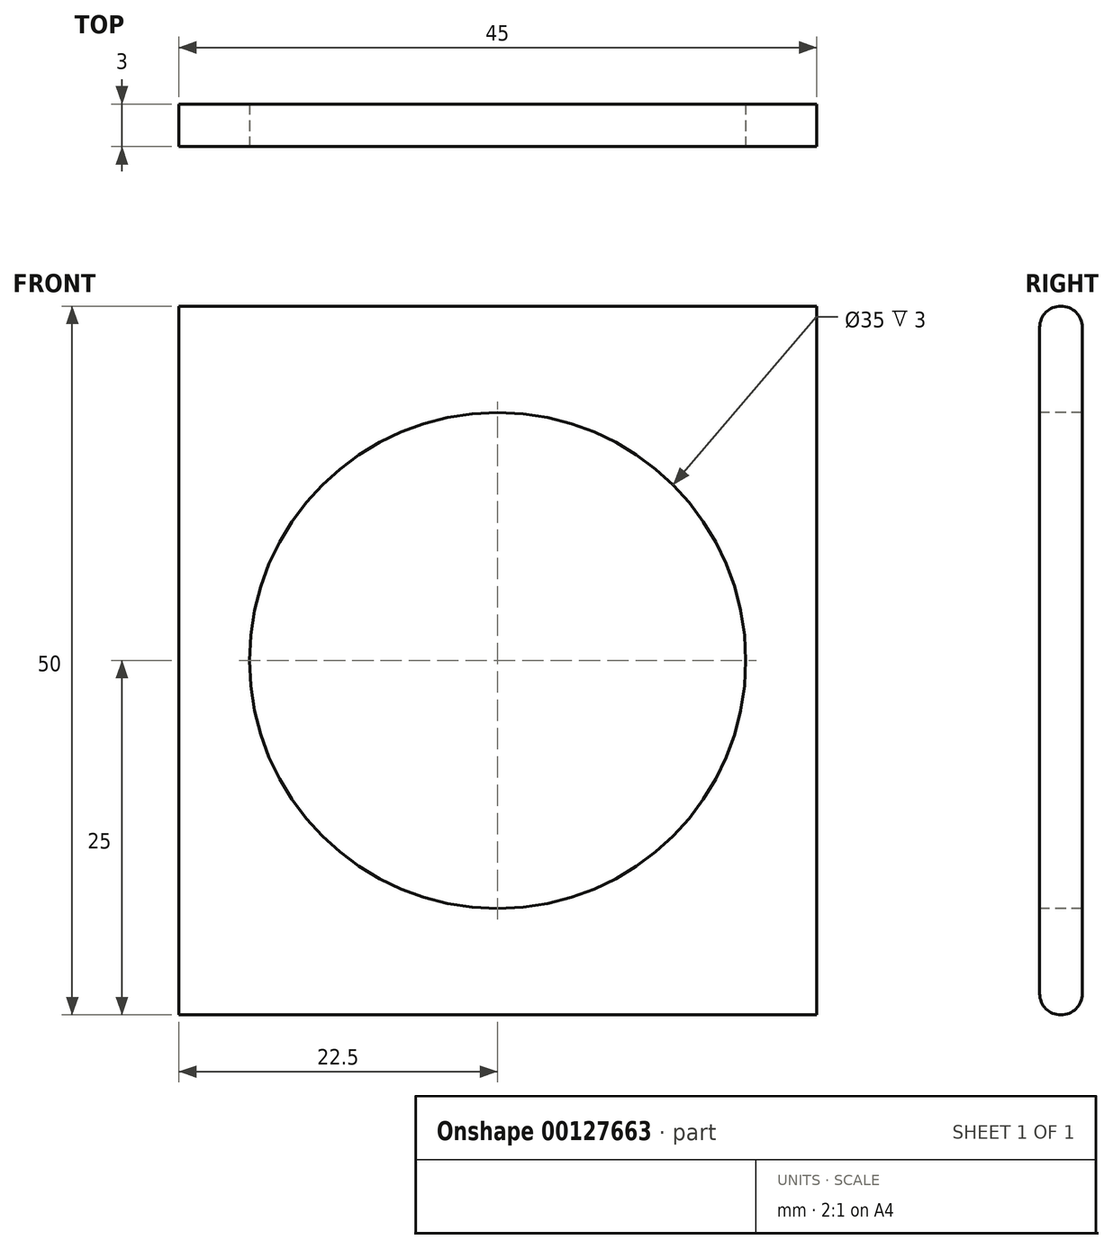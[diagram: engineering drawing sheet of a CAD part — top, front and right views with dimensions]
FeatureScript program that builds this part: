
annotation { "Feature Type Name" : "Feature", "Feature Type Description" : "" }
export const myFeature = defineFeature(function(context is Context, id is Id, definition is map)
    precondition{}
    {
        {
            var Q0;
            Q0=qCreatedBy(makeId("Right.planeOp"),FACE);
            var sketch = newSketch(context, id + "F0", { "sketchPlane" : qUnion([Q0])});
            skLineSegment(sketch, "E0", {"start": v(0, 25) * mm, "end": v(0, -25) * mm});
            skLineSegment(sketch, "E1", {"start": v(0, -25) * mm, "end": v(-3, -25) * mm});
            skLineSegment(sketch, "E2", {"start": v(-3, -25) * mm, "end": v(-3, -21.25) * mm});
            skLineSegment(sketch, "E3", {"start": v(-3, -21.25) * mm, "end": v(-9, -21.25) * mm});
            skLineSegment(sketch, "E4", {"start": v(-9, -21.25) * mm, "end": v(-9, 21.25) * mm});
            skLineSegment(sketch, "E5", {"start": v(-9, 21.25) * mm, "end": v(-3, 21.25) * mm});
            skLineSegment(sketch, "E6", {"start": v(-3, 21.25) * mm, "end": v(-3, 25) * mm});
            skLineSegment(sketch, "E7", {"start": v(-3, 25) * mm, "end": v(0, 25) * mm});
            skSolve(sketch);
        }
        {
            var Q0;
            Q0=qSketchRegion(id+"F0",true);
            extrude(context, id + "F1", {"entities" : qUnion([Q0]), "endBound" : BoundingType.SYMMETRIC, "depth" : 45 * mm});
        }
        {
            var Q0;
            Q0=makeQuery(id+"F1.opExtrude","SWEPT_FACE",FACE,{"disambiguationData":[OSD([sQuery(id+"F0.wireOp",EDGE,"E4")])]});
            var sketch = newSketch(context, id + "F2", { "sketchPlane" : qUnion([Q0])});
            skCircle(sketch, "E8", {"center": v(0, 0) * mm, "radius": 18.6 * mm});
            skSolve(sketch);
        }
        {
            var Q0;
            Q0=qSketchRegion(id+"F2",true);
            extrude(context, id + "F3", {"entities" : qUnion([Q0]), "operationType" : NewBodyOperationType.REMOVE, "oppositeDirection" : true, "depth" : 6 * mm});
        }
        {
            var Q0;
            Q0=makeQuery(id+"F3.boolean.opBoolean","COPY",FACE,{"derivedFrom":makeQuery(id+"F3.opExtrude","CAP_FACE",FACE,{"disambiguationData":[OSD([sQuery(id+"F2.wireOp",EDGE,"E8")])],"isStart":false})});
            var sketch = newSketch(context, id + "F4", { "sketchPlane" : qUnion([Q0])});
            skCircle(sketch, "E9", {"center": v(0, 0) * mm, "radius": 17.5 * mm});
            skSolve(sketch);
        }
        {
            var Q0;
            Q0=qSketchRegion(id+"F4",true);
            extrude(context, id + "F5", {"entities" : qUnion([Q0]), "operationType" : NewBodyOperationType.REMOVE, "endBound" : BoundingType.UP_TO_NEXT, "oppositeDirection" : true, "depth" : 25 * mm});
        }
        {
            var Q0;
            Q0=makeQuery(id+"F1.opExtrude","SWEPT_FACE",FACE,{"disambiguationData":[OSD([sQuery(id+"F0.wireOp",EDGE,"E4")])]});
            var sketch = newSketch(context, id + "F6", { "sketchPlane" : qUnion([Q0])});
            skLineSegment(sketch, "E10", {"start": v(0, 42.2) * mm, "end": v(0, -42.2) * mm, "construction": true});
            skLineSegment(sketch, "E11", {"start": v(-1.5, 21.05) * mm, "end": v(-1.68, 21.11) * mm});
            skLineSegment(sketch, "E12", {"start": v(-1.6, 25.84) * mm, "end": v(0.72, 26.6) * mm});
            skLineSegment(sketch, "E13", {"start": v(0.72, 28.5) * mm, "end": v(-3.1, 29.74) * mm});
            skLineSegment(sketch, "E14", {"start": v(-3.57, 34.29) * mm, "end": v(2.83, 37.92) * mm});
            skLineSegment(sketch, "E15", {"start": v(2.64, 39.74) * mm, "end": v(-4.93, 42.2) * mm});
            skLineSegment(sketch, "E16", {"start": v(-8.5, 31.5) * mm, "end": v(-8.5, 23.6) * mm, "construction": true});
            skLineSegment(sketch, "E17", {"start": v(-1.13, 24.41) * mm, "end": v(1.18, 25.17) * mm});
            skLineSegment(sketch, "E18", {"start": v(1.18, 29.92) * mm, "end": v(-2.64, 31.16) * mm});
            skLineSegment(sketch, "E19", {"start": v(-2.83, 32.99) * mm, "end": v(3.57, 36.61) * mm});
            skLineSegment(sketch, "E20", {"start": v(3.1, 41.17) * mm, "end": v(-0.08, 42.2) * mm});
            skLineSegment(sketch, "E21", {"start": v(8.5, 39.41) * mm, "end": v(8.5, 27.54) * mm, "construction": true});
            skLineSegment(sketch, "E22", {"start": v(-4.93, 42.2) * mm, "end": v(-0.08, 42.2) * mm});
            skPoint(sketch, "E23.visualSharp", {"position": v(-4.8, 31.87) * mm});
            skArc(sketch, "E23.filletArc", {"start": v(-2.83, 32.99) * mm, "mid": v(-3.33, 32.01) * mm, "end": v(-2.64, 31.16) * mm});
            skPoint(sketch, "E24.visualSharp", {"position": v(-4.56, 23.3) * mm});
            skArc(sketch, "E24.filletArc", {"start": v(-1.13, 24.41) * mm, "mid": v(-1.82, 23.48) * mm, "end": v(-1.16, 22.52) * mm});
            skPoint(sketch, "E25.visualSharp", {"position": v(3.65, 27.54) * mm});
            skArc(sketch, "E25.filletArc", {"start": v(0.72, 26.6) * mm, "mid": v(1.4, 27.54) * mm, "end": v(0.72, 28.5) * mm});
            skPoint(sketch, "E26.visualSharp", {"position": v(4.8, 39.04) * mm});
            skArc(sketch, "E26.filletArc", {"start": v(2.83, 37.92) * mm, "mid": v(3.33, 38.89) * mm, "end": v(2.64, 39.74) * mm});
            skPoint(sketch, "E27.visualSharp", {"position": v(8.5, 39.41) * mm});
            skArc(sketch, "E27.filletArc", {"start": v(3.57, 36.61) * mm, "mid": v(4.82, 39.04) * mm, "end": v(3.1, 41.17) * mm});
            skPoint(sketch, "E28.visualSharp", {"position": v(-8.5, 31.5) * mm});
            skArc(sketch, "E28.filletArc", {"start": v(-3.57, 34.29) * mm, "mid": v(-4.82, 31.86) * mm, "end": v(-3.1, 29.74) * mm});
            skPoint(sketch, "E29.visualSharp", {"position": v(8.5, 27.54) * mm});
            skArc(sketch, "E29.filletArc", {"start": v(1.18, 25.17) * mm, "mid": v(2.9, 27.54) * mm, "end": v(1.18, 29.92) * mm});
            skPoint(sketch, "E30.visualSharp", {"position": v(-8.5, 23.6) * mm});
            skArc(sketch, "E30.filletArc", {"start": v(-1.6, 25.84) * mm, "mid": v(-3.32, 23.5) * mm, "end": v(-1.68, 21.11) * mm});
            skLineSegment(sketch, "E31", {"start": v(0, 0) * mm, "end": v(22.5, 0) * mm, "construction": true});
            skArc(sketch, "E32.MirrorCS", {"start": v(-2.83, -32.99) * mm, "mid": v(-3.33, -32.01) * mm, "end": v(-2.64, -31.16) * mm});
            skArc(sketch, "E33.MirrorCS", {"start": v(2.83, -37.92) * mm, "mid": v(3.33, -38.89) * mm, "end": v(2.64, -39.74) * mm});
            skArc(sketch, "E34.MirrorCS", {"start": v(-1.13, -24.41) * mm, "mid": v(-1.82, -23.48) * mm, "end": v(-1.16, -22.52) * mm});
            skLineSegment(sketch, "E35.MirrorCS", {"start": v(3.1, -41.17) * mm, "end": v(-0.08, -42.2) * mm});
            skLineSegment(sketch, "E36.MirrorCS", {"start": v(-1.5, -21.05) * mm, "end": v(-1.68, -21.11) * mm});
            skArc(sketch, "E37.MirrorCS", {"start": v(0.72, -26.6) * mm, "mid": v(1.4, -27.54) * mm, "end": v(0.72, -28.5) * mm});
            skArc(sketch, "E38.MirrorCS", {"start": v(1.18, -25.17) * mm, "mid": v(2.9, -27.54) * mm, "end": v(1.18, -29.92) * mm});
            skArc(sketch, "E39.MirrorCS", {"start": v(3.57, -36.61) * mm, "mid": v(4.82, -39.04) * mm, "end": v(3.1, -41.17) * mm});
            skArc(sketch, "E40.MirrorCS", {"start": v(-3.57, -34.29) * mm, "mid": v(-4.82, -31.86) * mm, "end": v(-3.1, -29.74) * mm});
            skLineSegment(sketch, "E41.MirrorCS", {"start": v(-1.13, -24.41) * mm, "end": v(1.18, -25.17) * mm});
            skLineSegment(sketch, "E42.MirrorCS", {"start": v(-2.83, -32.99) * mm, "end": v(3.57, -36.61) * mm});
            skLineSegment(sketch, "E43.MirrorCS", {"start": v(2.64, -39.74) * mm, "end": v(-4.93, -42.2) * mm});
            skLineSegment(sketch, "E44.MirrorCS", {"start": v(-3.57, -34.29) * mm, "end": v(2.83, -37.92) * mm});
            skLineSegment(sketch, "E45.MirrorCS", {"start": v(0.72, -28.5) * mm, "end": v(-3.1, -29.74) * mm});
            skLineSegment(sketch, "E46.MirrorCS", {"start": v(-1.6, -25.84) * mm, "end": v(0.72, -26.6) * mm});
            skPoint(sketch, "E47.MirrorP", {"position": v(-4.56, -23.3) * mm});
            skPoint(sketch, "E48.MirrorP", {"position": v(4.8, -39.04) * mm});
            skLineSegment(sketch, "E49.MirrorCS", {"start": v(-4.93, -42.2) * mm, "end": v(-0.08, -42.2) * mm});
            skLineSegment(sketch, "E50.MirrorCS", {"start": v(1.18, -29.92) * mm, "end": v(-2.64, -31.16) * mm});
            skPoint(sketch, "E51.MirrorP", {"position": v(-8.5, -31.5) * mm});
            skPoint(sketch, "E52.MirrorP", {"position": v(8.5, -27.54) * mm});
            skPoint(sketch, "E53.MirrorP", {"position": v(3.65, -27.54) * mm});
            skPoint(sketch, "E54.MirrorP", {"position": v(8.5, -39.41) * mm});
            skPoint(sketch, "E55.MirrorP", {"position": v(-8.5, -23.6) * mm});
            skArc(sketch, "E56.MirrorCS", {"start": v(-1.6, -25.84) * mm, "mid": v(-3.32, -23.5) * mm, "end": v(-1.68, -21.11) * mm});
            skPoint(sketch, "E57.MirrorP", {"position": v(-4.8, -31.87) * mm});
            skPoint(sketch, "E58.orphan", {"position": v(1.5, 21.25) * mm});
            skLineSegment(sketch, "E59", {"start": v(-1.5, 21.05) * mm, "end": v(2.89, 21.05) * mm});
            skLineSegment(sketch, "E60", {"start": v(2.89, 21.05) * mm, "end": v(-1.16, 22.52) * mm});
            skLineSegment(sketch, "E61", {"start": v(-1.5, -21.05) * mm, "end": v(2.89, -21.05) * mm});
            skLineSegment(sketch, "E62", {"start": v(2.89, -21.05) * mm, "end": v(-1.16, -22.52) * mm});
            skSolve(sketch);
        }
        {
            var Q0;
            Q0=qSketchRegion(id+"F6",true);
            extrude(context, id + "F7", {"entities" : qUnion([Q0]), "operationType" : NewBodyOperationType.ADD, "oppositeDirection" : true, "depth" : 3 * mm});
        }
        {
            var Q0;
            Q0=makeQuery(id+"F7.boolean.opBoolean","MERGE",FACE,{"derivedFrom":[makeQuery(id+"F1.opExtrude","SWEPT_FACE",FACE,{"disambiguationData":[OSD([sQuery(id+"F0.wireOp",EDGE,"E4")])]}),makeQuery(id+"F7.opExtrude","CAP_FACE",FACE,{"disambiguationData":[OSD([sQuery(id+"F6.wireOp",EDGE,"E11"),sQuery(id+"F6.wireOp",EDGE,"E12"),sQuery(id+"F6.wireOp",EDGE,"E13"),sQuery(id+"F6.wireOp",EDGE,"E14"),sQuery(id+"F6.wireOp",EDGE,"E15"),sQuery(id+"F6.wireOp",EDGE,"E17"),sQuery(id+"F6.wireOp",EDGE,"E18"),sQuery(id+"F6.wireOp",EDGE,"E19"),sQuery(id+"F6.wireOp",EDGE,"E20"),sQuery(id+"F6.wireOp",EDGE,"E22"),sQuery(id+"F6.wireOp",EDGE,"E23.filletArc"),sQuery(id+"F6.wireOp",EDGE,"E24.filletArc"),sQuery(id+"F6.wireOp",EDGE,"E25.filletArc"),sQuery(id+"F6.wireOp",EDGE,"E26.filletArc"),sQuery(id+"F6.wireOp",EDGE,"E27.filletArc"),sQuery(id+"F6.wireOp",EDGE,"E28.filletArc"),sQuery(id+"F6.wireOp",EDGE,"E29.filletArc"),sQuery(id+"F6.wireOp",EDGE,"E30.filletArc"),sQuery(id+"F6.wireOp",EDGE,"E59"),sQuery(id+"F6.wireOp",EDGE,"E60")])],"isStart":true}),makeQuery(id+"F7.opExtrude","CAP_FACE",FACE,{"disambiguationData":[OSD([sQuery(id+"F6.wireOp",EDGE,"E32.MirrorCS"),sQuery(id+"F6.wireOp",EDGE,"E33.MirrorCS"),sQuery(id+"F6.wireOp",EDGE,"E34.MirrorCS"),sQuery(id+"F6.wireOp",EDGE,"E35.MirrorCS"),sQuery(id+"F6.wireOp",EDGE,"E36.MirrorCS"),sQuery(id+"F6.wireOp",EDGE,"E37.MirrorCS"),sQuery(id+"F6.wireOp",EDGE,"E38.MirrorCS"),sQuery(id+"F6.wireOp",EDGE,"E39.MirrorCS"),sQuery(id+"F6.wireOp",EDGE,"E40.MirrorCS"),sQuery(id+"F6.wireOp",EDGE,"E41.MirrorCS"),sQuery(id+"F6.wireOp",EDGE,"E42.MirrorCS"),sQuery(id+"F6.wireOp",EDGE,"E43.MirrorCS"),sQuery(id+"F6.wireOp",EDGE,"E44.MirrorCS"),sQuery(id+"F6.wireOp",EDGE,"E45.MirrorCS"),sQuery(id+"F6.wireOp",EDGE,"E46.MirrorCS"),sQuery(id+"F6.wireOp",EDGE,"E49.MirrorCS"),sQuery(id+"F6.wireOp",EDGE,"E50.MirrorCS"),sQuery(id+"F6.wireOp",EDGE,"E56.MirrorCS"),sQuery(id+"F6.wireOp",EDGE,"E61"),sQuery(id+"F6.wireOp",EDGE,"E62")])],"isStart":true})]});
            var sketch = newSketch(context, id + "F12", { "sketchPlane" : qUnion([Q0])});
            skLineSegment(sketch, "E63", {"start": v(-10, 41.7) * mm, "end": v(5, 41.7) * mm});
            skLineSegment(sketch, "E64", {"start": v(-10, 41.7) * mm, "end": v(-10, 45.1) * mm});
            skLineSegment(sketch, "E65", {"start": v(5, 45.1) * mm, "end": v(5, 41.7) * mm});
            skArc(sketch, "E66", {"start": v(4.86, 45.45) * mm, "mid": v(-2.5, 48.69) * mm, "end": v(-9.87, 45.45) * mm});
            skLineSegment(sketch, "E67", {"start": v(-2.5, 42.2) * mm, "end": v(-2.5, 41.7) * mm});
            skPoint(sketch, "E68.visualSharp", {"position": v(-11.33, 62.8) * mm});
            skPoint(sketch, "E69.visualSharp", {"position": v(-10, 45.3) * mm});
            skArc(sketch, "E69.filletArc", {"start": v(-9.87, 45.45) * mm, "mid": v(-9.97, 45.29) * mm, "end": v(-10, 45.1) * mm});
            skPoint(sketch, "E70.visualSharp", {"position": v(5, 45.3) * mm});
            skArc(sketch, "E70.filletArc", {"start": v(5, 45.1) * mm, "mid": v(4.96, 45.29) * mm, "end": v(4.86, 45.45) * mm});
            skLineSegment(sketch, "E71", {"start": v(0, 0) * mm, "end": v(18.6, 0) * mm, "construction": true});
            skLineSegment(sketch, "E72.MirrorCS", {"start": v(-10, -41.7) * mm, "end": v(5, -41.7) * mm});
            skArc(sketch, "E73.MirrorCS", {"start": v(4.86, -45.45) * mm, "mid": v(-2.5, -48.69) * mm, "end": v(-9.87, -45.45) * mm});
            skLineSegment(sketch, "E74.MirrorCS", {"start": v(-10, -41.7) * mm, "end": v(-10, -45.1) * mm});
            skLineSegment(sketch, "E75.MirrorCS", {"start": v(5, -45.1) * mm, "end": v(5, -41.7) * mm});
            skArc(sketch, "E76.MirrorCS", {"start": v(5, -45.1) * mm, "mid": v(4.96, -45.29) * mm, "end": v(4.86, -45.45) * mm});
            skArc(sketch, "E77.MirrorCS", {"start": v(-9.87, -45.45) * mm, "mid": v(-9.97, -45.29) * mm, "end": v(-10, -45.1) * mm});
            skLineSegment(sketch, "E78", {"start": v(-2.5, 45.1) * mm, "end": v(-2.5, 48.69) * mm, "construction": true});
            skLineSegment(sketch, "E79", {"start": v(-2.5, 45.1) * mm, "end": v(-10, 45.1) * mm, "construction": true});
            skSolve(sketch);
        }
        {
            var Q0;
            Q0=qSketchRegion(id+"F12",true);
            extrude(context, id + "F8", {"entities" : qUnion([Q0]), "operationType" : NewBodyOperationType.ADD, "oppositeDirection" : true, "depth" : 3 * mm});
        }
        {
            var Q0;
            Q0=makeQuery(id+"F8.boolean.opBoolean","MERGE",FACE,{"derivedFrom":[makeQuery(id+"F7.opExtrude","CAP_FACE",FACE,{"disambiguationData":[OSD([sQuery(id+"F6.wireOp",EDGE,"E11"),sQuery(id+"F6.wireOp",EDGE,"E12"),sQuery(id+"F6.wireOp",EDGE,"E13"),sQuery(id+"F6.wireOp",EDGE,"E14"),sQuery(id+"F6.wireOp",EDGE,"E15"),sQuery(id+"F6.wireOp",EDGE,"E17"),sQuery(id+"F6.wireOp",EDGE,"E18"),sQuery(id+"F6.wireOp",EDGE,"E19"),sQuery(id+"F6.wireOp",EDGE,"E20"),sQuery(id+"F6.wireOp",EDGE,"E22"),sQuery(id+"F6.wireOp",EDGE,"E23.filletArc"),sQuery(id+"F6.wireOp",EDGE,"E24.filletArc"),sQuery(id+"F6.wireOp",EDGE,"E25.filletArc"),sQuery(id+"F6.wireOp",EDGE,"E26.filletArc"),sQuery(id+"F6.wireOp",EDGE,"E27.filletArc"),sQuery(id+"F6.wireOp",EDGE,"E28.filletArc"),sQuery(id+"F6.wireOp",EDGE,"E29.filletArc"),sQuery(id+"F6.wireOp",EDGE,"E30.filletArc"),sQuery(id+"F6.wireOp",EDGE,"E59"),sQuery(id+"F6.wireOp",EDGE,"E60")])],"isStart":false}),makeQuery(id+"F8.opExtrude","CAP_FACE",FACE,{"disambiguationData":[OSD([sQuery(id+"F12.wireOp",EDGE,"E63"),sQuery(id+"F12.wireOp",EDGE,"E64"),sQuery(id+"F12.wireOp",EDGE,"E65"),sQuery(id+"F12.wireOp",EDGE,"E66"),sQuery(id+"F12.wireOp",EDGE,"E69.filletArc"),sQuery(id+"F12.wireOp",EDGE,"E70.filletArc")])],"isStart":false})]});
            var sketch = newSketch(context, id + "F13", { "sketchPlane" : qUnion([Q0])});
            skLineSegment(sketch, "E80", {"start": v(10, 41.7) * mm, "end": v(10, 41.9) * mm});
            skLineSegment(sketch, "E81", {"start": v(10, 41.9) * mm, "end": v(9, 42.9) * mm});
            skLineSegment(sketch, "E82", {"start": v(9, 42.9) * mm, "end": v(8, 41.9) * mm});
            skLineSegment(sketch, "E83", {"start": v(8, 41.9) * mm, "end": v(7, 42.9) * mm});
            skLineSegment(sketch, "E84", {"start": v(7, 42.9) * mm, "end": v(6, 41.9) * mm});
            skLineSegment(sketch, "E85", {"start": v(6, 41.9) * mm, "end": v(5, 42.9) * mm});
            skLineSegment(sketch, "E86", {"start": v(4, 41.9) * mm, "end": v(5, 42.9) * mm});
            skLineSegment(sketch, "E87", {"start": v(4, 41.9) * mm, "end": v(3, 42.9) * mm});
            skLineSegment(sketch, "E88", {"start": v(3, 42.9) * mm, "end": v(2, 41.9) * mm});
            skLineSegment(sketch, "E89", {"start": v(2, 41.9) * mm, "end": v(1, 42.9) * mm});
            skLineSegment(sketch, "E90", {"start": v(1, 42.9) * mm, "end": v(0, 41.9) * mm});
            skLineSegment(sketch, "E91", {"start": v(0, 41.9) * mm, "end": v(-1, 42.9) * mm});
            skLineSegment(sketch, "E92", {"start": v(-1, 42.9) * mm, "end": v(-2, 41.9) * mm});
            skLineSegment(sketch, "E93", {"start": v(-2, 41.9) * mm, "end": v(-3, 42.9) * mm});
            skLineSegment(sketch, "E94", {"start": v(-3, 42.9) * mm, "end": v(-4, 41.9) * mm});
            skLineSegment(sketch, "E95", {"start": v(-4, 41.9) * mm, "end": v(-5, 42.9) * mm});
            skLineSegment(sketch, "E96", {"start": v(-5, 42.9) * mm, "end": v(-5, 41.7) * mm});
            skPoint(sketch, "E97.end.orphan", {"position": v(-6, 41.9) * mm});
            skLineSegment(sketch, "E98", {"start": v(10, 41.7) * mm, "end": v(-5, 41.7) * mm});
            skLineSegment(sketch, "E99", {"start": v(0, 0) * mm, "end": v(17.5, 0) * mm, "construction": true});
            skLineSegment(sketch, "E100.MirrorCS", {"start": v(-5, -42.9) * mm, "end": v(-5, -41.7) * mm});
            skLineSegment(sketch, "E101.MirrorCS", {"start": v(-4, -41.9) * mm, "end": v(-5, -42.9) * mm});
            skLineSegment(sketch, "E102.MirrorCS", {"start": v(10, -41.7) * mm, "end": v(-5, -41.7) * mm});
            skLineSegment(sketch, "E103.MirrorCS", {"start": v(-3, -42.9) * mm, "end": v(-4, -41.9) * mm});
            skLineSegment(sketch, "E104.MirrorCS", {"start": v(-2, -41.9) * mm, "end": v(-3, -42.9) * mm});
            skLineSegment(sketch, "E105.MirrorCS", {"start": v(-1, -42.9) * mm, "end": v(-2, -41.9) * mm});
            skLineSegment(sketch, "E106.MirrorCS", {"start": v(0, -41.9) * mm, "end": v(-1, -42.9) * mm});
            skLineSegment(sketch, "E107.MirrorCS", {"start": v(1, -42.9) * mm, "end": v(0, -41.9) * mm});
            skLineSegment(sketch, "E108.MirrorCS", {"start": v(2, -41.9) * mm, "end": v(1, -42.9) * mm});
            skLineSegment(sketch, "E109.MirrorCS", {"start": v(3, -42.9) * mm, "end": v(2, -41.9) * mm});
            skLineSegment(sketch, "E110.MirrorCS", {"start": v(4, -41.9) * mm, "end": v(3, -42.9) * mm});
            skLineSegment(sketch, "E111.MirrorCS", {"start": v(4, -41.9) * mm, "end": v(5, -42.9) * mm});
            skLineSegment(sketch, "E112.MirrorCS", {"start": v(6, -41.9) * mm, "end": v(5, -42.9) * mm});
            skLineSegment(sketch, "E113.MirrorCS", {"start": v(8, -41.9) * mm, "end": v(7, -42.9) * mm});
            skLineSegment(sketch, "E114.MirrorCS", {"start": v(7, -42.9) * mm, "end": v(6, -41.9) * mm});
            skLineSegment(sketch, "E115.MirrorCS", {"start": v(9, -42.9) * mm, "end": v(8, -41.9) * mm});
            skLineSegment(sketch, "E116.MirrorCS", {"start": v(10, -41.9) * mm, "end": v(9, -42.9) * mm});
            skLineSegment(sketch, "E117.MirrorCS", {"start": v(10, -41.7) * mm, "end": v(10, -41.9) * mm});
            skSolve(sketch);
        }
        {
            var Q0;
            Q0=qSketchRegion(id+"F13",true);
            extrude(context, id + "F14", {"entities" : qUnion([Q0]), "operationType" : NewBodyOperationType.ADD, "depth" : 3 * mm});
        }
        {
            var Q0;
            Q0=makeQuery(id+"F7.boolean.opBoolean","INTERSECT",EDGE,{"derivedFrom":[makeQuery(id+"F1.opExtrude","SWEPT_FACE",FACE,{"disambiguationData":[OSD([sQuery(id+"F0.wireOp",EDGE,"E5")])]}),makeQuery(id+"F7.opExtrude","SWEPT_FACE",FACE,{"disambiguationData":[OSD([sQuery(id+"F6.wireOp",EDGE,"E30.filletArc")])]})]});
            var Q1;
            Q1=makeQuery(id+"F7.boolean.opBoolean","INTERSECT",EDGE,{"derivedFrom":[makeQuery(id+"F1.opExtrude","SWEPT_FACE",FACE,{"disambiguationData":[OSD([sQuery(id+"F0.wireOp",EDGE,"E5")])]}),makeQuery(id+"F7.opExtrude","SWEPT_FACE",FACE,{"disambiguationData":[OSD([sQuery(id+"F6.wireOp",EDGE,"E60")])]})]});
            var Q2;
            Q2=makeQuery(id+"F8.boolean.opBoolean","INTERSECT",EDGE,{"derivedFrom":[makeQuery(id+"F7.opExtrude","SWEPT_FACE",FACE,{"disambiguationData":[OSD([sQuery(id+"F6.wireOp",EDGE,"E15")])]}),makeQuery(id+"F8.opExtrude","SWEPT_FACE",FACE,{"disambiguationData":[OSD([sQuery(id+"F12.wireOp",EDGE,"E63")])]})]});
            var Q3;
            Q3=makeQuery(id+"F8.boolean.opBoolean","INTERSECT",EDGE,{"derivedFrom":[makeQuery(id+"F7.opExtrude","SWEPT_FACE",FACE,{"disambiguationData":[OSD([sQuery(id+"F6.wireOp",EDGE,"E20")])]}),makeQuery(id+"F8.opExtrude","SWEPT_FACE",FACE,{"disambiguationData":[OSD([sQuery(id+"F12.wireOp",EDGE,"E63")])]})]});
            var Q4;
            Q4=makeQuery(id+"F7.boolean.opBoolean","INTERSECT",EDGE,{"derivedFrom":[makeQuery(id+"F1.opExtrude","SWEPT_FACE",FACE,{"disambiguationData":[OSD([sQuery(id+"F0.wireOp",EDGE,"E3")])]}),makeQuery(id+"F7.opExtrude","SWEPT_FACE",FACE,{"disambiguationData":[OSD([sQuery(id+"F6.wireOp",EDGE,"E56.MirrorCS")])]})]});
            var Q5;
            Q5=makeQuery(id+"F8.boolean.opBoolean","INTERSECT",EDGE,{"derivedFrom":[makeQuery(id+"F7.opExtrude","SWEPT_FACE",FACE,{"disambiguationData":[OSD([sQuery(id+"F6.wireOp",EDGE,"E43.MirrorCS")])]}),makeQuery(id+"F8.opExtrude","SWEPT_FACE",FACE,{"disambiguationData":[OSD([sQuery(id+"F12.wireOp",EDGE,"E72.MirrorCS")])]})]});
            var Q6;
            Q6=makeQuery(id+"F7.boolean.opBoolean","INTERSECT",EDGE,{"derivedFrom":[makeQuery(id+"F1.opExtrude","SWEPT_FACE",FACE,{"disambiguationData":[OSD([sQuery(id+"F0.wireOp",EDGE,"E3")])]}),makeQuery(id+"F7.opExtrude","SWEPT_FACE",FACE,{"disambiguationData":[OSD([sQuery(id+"F6.wireOp",EDGE,"E62")])]})]});
            var Q7;
            Q7=makeQuery(id+"F8.boolean.opBoolean","INTERSECT",EDGE,{"derivedFrom":[makeQuery(id+"F7.opExtrude","SWEPT_FACE",FACE,{"disambiguationData":[OSD([sQuery(id+"F6.wireOp",EDGE,"E35.MirrorCS")])]}),makeQuery(id+"F8.opExtrude","SWEPT_FACE",FACE,{"disambiguationData":[OSD([sQuery(id+"F12.wireOp",EDGE,"E72.MirrorCS")])]})]});
            fillet(context, id + "F9", {"entities" : qUnion([Q0, Q1, Q2, Q3, Q4, Q5, Q6, Q7]), "radius" : 1 * mm, "tangentPropagation" : true, "allowEdgeOverflow" : false});
        }
        {
            var Q0;
            Q0=makeQuery(id+"F1.opExtrude","CAP_FACE",FACE,{"disambiguationData":[OSD([sQuery(id+"F0.wireOp",EDGE,"E0"),sQuery(id+"F0.wireOp",EDGE,"E1"),sQuery(id+"F0.wireOp",EDGE,"E2"),sQuery(id+"F0.wireOp",EDGE,"E3"),sQuery(id+"F0.wireOp",EDGE,"E4"),sQuery(id+"F0.wireOp",EDGE,"E5"),sQuery(id+"F0.wireOp",EDGE,"E6"),sQuery(id+"F0.wireOp",EDGE,"E7")])],"isStart":false});
            var sketch = newSketch(context, id + "F15", { "sketchPlane" : qUnion([Q0])});
            skLineSegment(sketch, "E118.bottom", {"start": v(-9, 48.7) * mm, "end": v(-3, 48.7) * mm});
            skLineSegment(sketch, "E118.top", {"start": v(-9, -48.7) * mm, "end": v(-3, -48.7) * mm});
            skLineSegment(sketch, "E118.left", {"start": v(-9, 48.7) * mm, "end": v(-9, -48.7) * mm});
            skLineSegment(sketch, "E118.right", {"start": v(-3, 48.7) * mm, "end": v(-3, -48.7) * mm});
            skSolve(sketch);
        }
        {
            var Q0;
            Q0 = qSketchRegion(id + "F15", true);
            extrude(context, id + "F10", {"entities" : qUnion([Q0]), "operationType" : NewBodyOperationType.REMOVE, "endBound" : BoundingType.THROUGH_ALL, "oppositeDirection" : true, "depth" : 25 * mm});
        }
        {
            var Q0;
            Q0=makeQuery(id+"F1.opExtrude","SWEPT_EDGE",EDGE,{"disambiguationData":[OSD([sQuery(id+"F0.wireOp",EDGE,"E6"),sQuery(id+"F0.wireOp",EDGE,"E7")])]});
            var Q1;
            Q1=makeQuery(id+"F1.opExtrude","SWEPT_EDGE",EDGE,{"disambiguationData":[OSD([sQuery(id+"F0.wireOp",EDGE,"E0"),sQuery(id+"F0.wireOp",EDGE,"E7")])]});
            var Q2;
            Q2=makeQuery(id+"F1.opExtrude","SWEPT_EDGE",EDGE,{"disambiguationData":[OSD([sQuery(id+"F0.wireOp",EDGE,"E1"),sQuery(id+"F0.wireOp",EDGE,"E2")])]});
            var Q3;
            Q3=makeQuery(id+"F1.opExtrude","SWEPT_EDGE",EDGE,{"disambiguationData":[OSD([sQuery(id+"F0.wireOp",EDGE,"E0"),sQuery(id+"F0.wireOp",EDGE,"E1")])]});
            fillet(context, id + "F11", {"entities" : qUnion([Q0, Q1, Q2, Q3]), "radius" : 1.5 * mm, "tangentPropagation" : true, "allowEdgeOverflow" : false});
        }
    });
